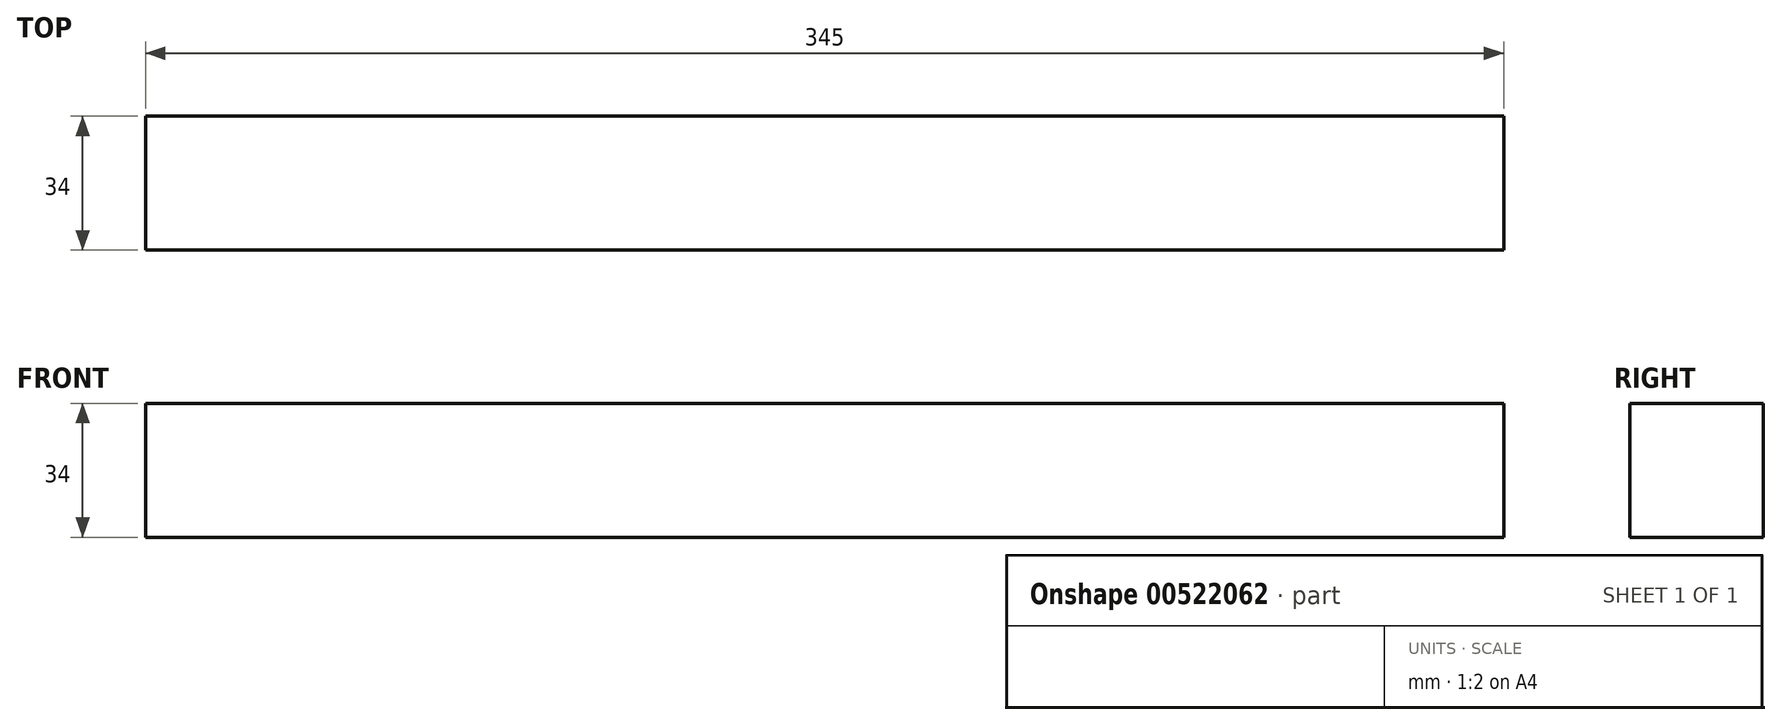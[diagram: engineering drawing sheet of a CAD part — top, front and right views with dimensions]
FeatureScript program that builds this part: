
annotation { "Feature Type Name" : "Feature", "Feature Type Description" : "" }
export const myFeature = defineFeature(function(context is Context, id is Id, definition is map)
    precondition{}
    {
        {
            var Q0;
            Q0=qCreatedBy(makeId("Right.planeOp"),FACE);
            var sketch = newSketch(context, id + "F0", { "sketchPlane" : qUnion([Q0])});
            skLineSegment(sketch, "E0.bottom", {"start": v(0, 0) * mm, "end": v(-34, 0) * mm});
            skLineSegment(sketch, "E0.top", {"start": v(0, 34) * mm, "end": v(-34, 34) * mm});
            skLineSegment(sketch, "E0.left", {"start": v(0, 0) * mm, "end": v(0, 34) * mm});
            skLineSegment(sketch, "E0.right", {"start": v(-34, 0) * mm, "end": v(-34, 34) * mm});
            skSolve(sketch);
        }
        {
            var Q0;
            Q0=makeQuery(id+"F0.imprint","IMPRINT",FACE,{"disambiguationData":[TD([[makeQuery(id+"F0.imprint","IMPRINT",EDGE,{"derivedFrom":sQuery(id+"F0.wireOp",EDGE,"E0.bottom")}),-1.0]])]});
            extrude(context, id + "F1", {"entities" : qUnion([Q0]), "oppositeDirection" : true, "depth" : (411 - 100 + 34) * mm, "offsetDistance" : 25 * mm});
        }
    });
